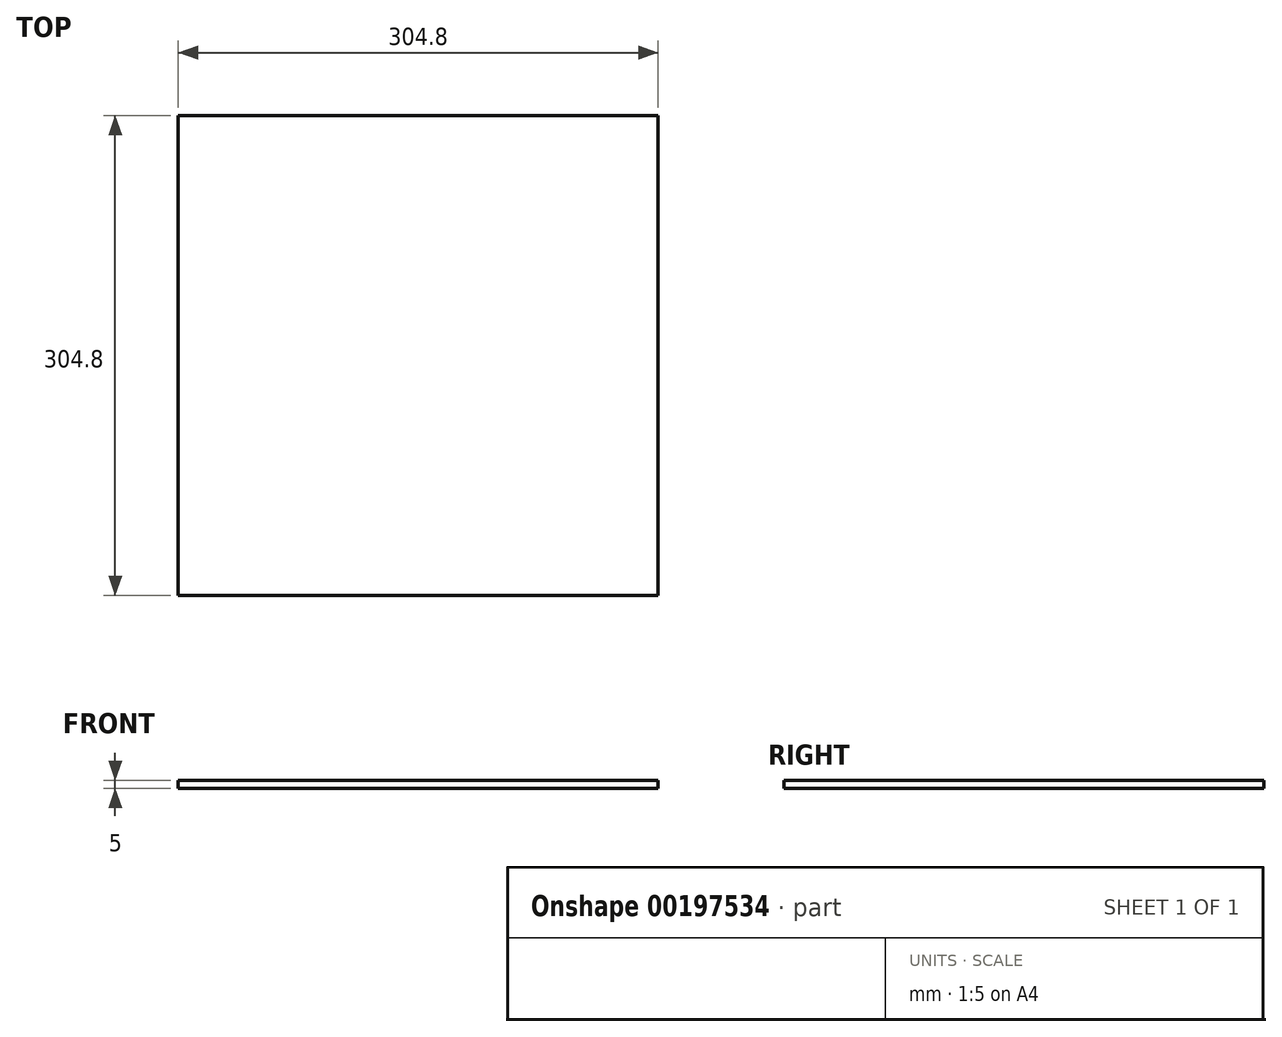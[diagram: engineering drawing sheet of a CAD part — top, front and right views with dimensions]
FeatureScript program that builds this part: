
annotation { "Feature Type Name" : "Feature", "Feature Type Description" : "" }
export const myFeature = defineFeature(function(context is Context, id is Id, definition is map)
    precondition{}
    {
        {
            var Q0;
            Q0=qCreatedBy(makeId("Top.planeOp"),FACE);
            var sketch = newSketch(context, id + "F0", { "sketchPlane" : qUnion([Q0])});
            skLineSegment(sketch, "E0.bottom", {"start": v(-152.4, 152.4) * mm, "end": v(152.4, 152.4) * mm});
            skLineSegment(sketch, "E0.top", {"start": v(-152.4, -152.4) * mm, "end": v(152.4, -152.4) * mm});
            skLineSegment(sketch, "E0.left", {"start": v(-152.4, 152.4) * mm, "end": v(-152.4, -152.4) * mm});
            skLineSegment(sketch, "E0.right", {"start": v(152.4, 152.4) * mm, "end": v(152.4, -152.4) * mm});
            skSolve(sketch);
        }
        {
            var Q0;
            Q0=qSketchRegion(id+"F0",true);
            extrude(context, id + "F1", {"entities" : qUnion([Q0]), "depth" : 5 * mm});
        }
    });
